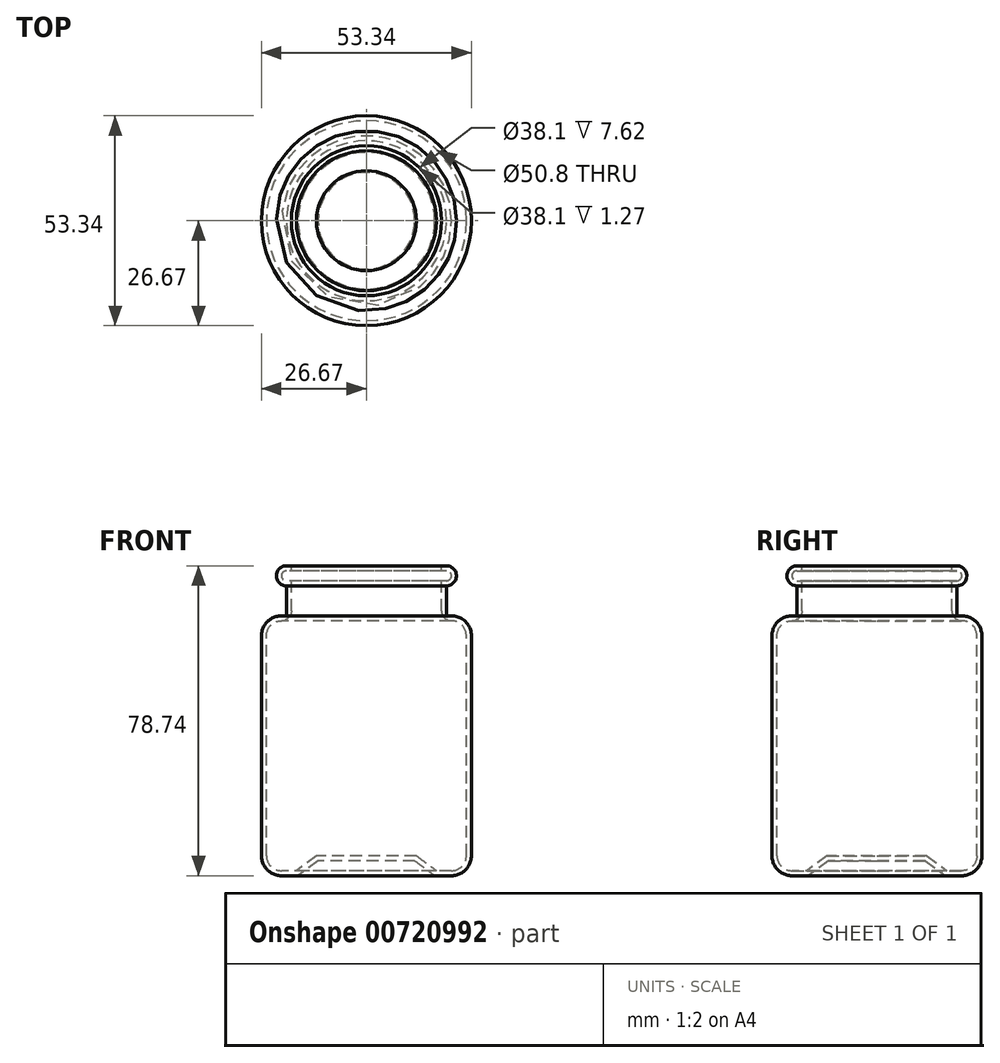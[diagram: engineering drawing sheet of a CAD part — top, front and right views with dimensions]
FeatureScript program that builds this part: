
annotation { "Feature Type Name" : "Feature", "Feature Type Description" : "" }
export const myFeature = defineFeature(function(context is Context, id is Id, definition is map)
    precondition{}
    {
        {
            var Q0;
            Q0=qCreatedBy(makeId("Front.planeOp"),FACE);
            var sketch = newSketch(context, id + "F0", { "sketchPlane" : qUnion([Q0])});
            skLineSegment(sketch, "E0", {"start": v(0, 0) * mm, "end": v(12.7, 0) * mm});
            skLineSegment(sketch, "E1", {"start": v(12.7, 0) * mm, "end": v(17.78, -3.81) * mm});
            skLineSegment(sketch, "E2", {"start": v(17.78, -3.81) * mm, "end": v(21.59, -3.81) * mm});
            skLineSegment(sketch, "E3", {"start": v(25.4, 0) * mm, "end": v(25.4, 55.88) * mm});
            skLineSegment(sketch, "E4", {"start": v(21.59, 59.7) * mm, "end": v(21.59, 59.7) * mm});
            skLineSegment(sketch, "E5", {"start": v(19.05, 62.23) * mm, "end": v(19.05, 69.85) * mm});
            skLineSegment(sketch, "E6", {"start": v(19.05, 69.85) * mm, "end": v(20.32, 69.85) * mm});
            skLineSegment(sketch, "E7", {"start": v(21.59, 71.12) * mm, "end": v(21.59, 71.12) * mm});
            skLineSegment(sketch, "E8", {"start": v(0, 0) * mm, "end": v(0, -55.9) * mm, "construction": true});
            skPoint(sketch, "E9.visualSharp", {"position": v(25.4, -3.81) * mm});
            skArc(sketch, "E9.filletArc", {"start": v(21.59, -3.8) * mm, "mid": v(24.28, -2.7) * mm, "end": v(25.4, 0) * mm});
            skPoint(sketch, "E10.visualSharp", {"position": v(25.4, 59.7) * mm});
            skArc(sketch, "E10.filletArc", {"start": v(25.4, 55.88) * mm, "mid": v(24.28, 58.57) * mm, "end": v(21.59, 59.7) * mm});
            skPoint(sketch, "E11.visualSharp", {"position": v(19.05, 59.7) * mm});
            skArc(sketch, "E11.filletArc", {"start": v(19.05, 62.23) * mm, "mid": v(19.8, 60.43) * mm, "end": v(21.59, 59.7) * mm});
            skPoint(sketch, "E12.visualSharp", {"position": v(21.59, 69.85) * mm});
            skArc(sketch, "E12.filletArc", {"start": v(20.32, 69.85) * mm, "mid": v(21.22, 70.22) * mm, "end": v(21.59, 71.12) * mm});
            skPoint(sketch, "E13.visualSharp", {"position": v(21.59, 72.37) * mm});
            skArc(sketch, "E13.filletArc", {"start": v(21.59, 71.12) * mm, "mid": v(21.22, 72.02) * mm, "end": v(20.32, 72.4) * mm});
            skLineSegment(sketch, "E14", {"start": v(20.32, 72.4) * mm, "end": v(19.05, 72.4) * mm});
            skLineSegment(sketch, "E15.0", {"start": v(20.32, 73.66) * mm, "end": v(19.05, 73.66) * mm});
            skArc(sketch, "E15.1", {"start": v(22.86, 71.02) * mm, "mid": v(22.15, 72.88) * mm, "end": v(20.32, 73.66) * mm});
            skArc(sketch, "E15.2", {"start": v(20.32, 68.58) * mm, "mid": v(22.08, 69.29) * mm, "end": v(22.86, 71.02) * mm});
            skLineSegment(sketch, "E15.3", {"start": v(20.32, 60.8) * mm, "end": v(20.32, 68.58) * mm});
            skArc(sketch, "E15.4", {"start": v(26.67, 55.88) * mm, "mid": v(24.7, 59.9) * mm, "end": v(20.32, 60.8) * mm});
            skLineSegment(sketch, "E15.5", {"start": v(26.67, 0) * mm, "end": v(26.67, 55.88) * mm});
            skLineSegment(sketch, "E15.6", {"start": v(0, -1.27) * mm, "end": v(12.28, -1.27) * mm});
            skLineSegment(sketch, "E15.7", {"start": v(12.28, -1.27) * mm, "end": v(17.36, -5.08) * mm});
            skLineSegment(sketch, "E15.8", {"start": v(17.36, -5.08) * mm, "end": v(21.6, -5.08) * mm});
            skArc(sketch, "E15.9", {"start": v(21.6, -5.08) * mm, "mid": v(25.18, -3.6) * mm, "end": v(26.67, 0) * mm});
            skLineSegment(sketch, "E16", {"start": v(19.05, 72.4) * mm, "end": v(19.05, 73.66) * mm});
            skLineSegment(sketch, "E17", {"start": v(0, 0) * mm, "end": v(0, -1.27) * mm});
            skSolve(sketch);
        }
        {
            var Q0;
            Q0 = qSketchRegion(id + "F0", true);
            var Q1;
            Q1=sQuery(id+"F0.wireOp",EDGE,"E8");
            revolve(context, id + "F1", {"surfaceOperationType" : NewSurfaceOperationType.NEW, "entities" : qUnion([Q0]), "axis" : qUnion([Q1]), "revolveType" : RevolveType.FULL});
        }
    });
